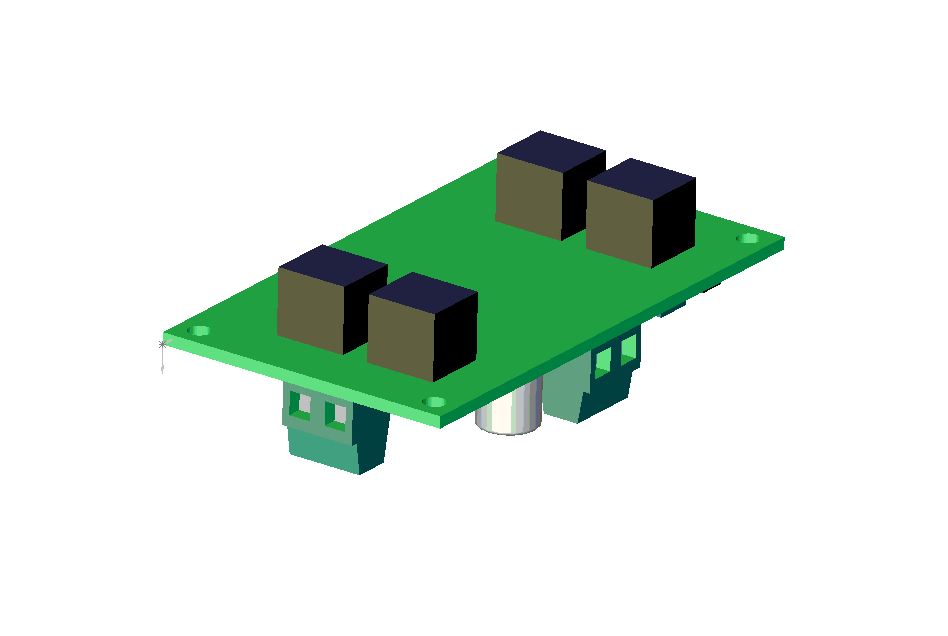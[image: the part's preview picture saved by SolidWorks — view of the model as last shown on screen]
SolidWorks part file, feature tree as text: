
SOLIDWORKS PART (.sldprt)
format: sldprt  version: not decoded by parser v0  size: 579,072 bytes
history: native  units: mm
features: sketch x24, extrude x15, cut_extrude x9, fillet x1, chamfer x1 (+8 scaffold rows collapsed)
feature tree (58):
  scaffold x8  (default folders/planes/origin — collapsed)
  sketch  "Sketch1"  dims[c1.D3=3.048mm c1.D4=3.05mm c1.D5=3.05mm c1.D6=3.05mm c2.D3=3.05mm c2.D1=69.0mm c2.D2=40.15mm c2.D7=3.05mm c2.D8=3.05mm c2.D9=3.05mm c2.D10=3.05mm]
  extrude  "Base-Extrude"  Depth=1.5748mm
  sketch  "Sketch2"  dims[c1.D1=12.7mm c1.D2=10.1mm c1.D3=10.1mm c1.D4=10.1mm c1.D5=8.1mm c1.D6=8.1mm c1.D7=8.1mm c1.D8=12.7mm c1.D9=28.5mm c2.D5=0.1mm c2.D6=0.1mm c2.D10=0.1mm c2.D11=8.0mm c2.D7=8.0mm c2.D12=8.0mm]
  extrude  "Boss-Extrude1"  Depth=9.94mm
  sketch  "Sketch3"  dims[c1.D1=4.3mm c1.D2=0.96mm c1.D3=1.7mm c1.D4=7.5mm c1.D5=1.45mm c1.D6=1.45mm c1.D7=7.5mm c1.D8=0.96mm c1.D9=0.96mm c2.D9=90.0deg c3.D9=1.7mm c3.D10=4.3mm]
  cut_extrude  "Cut-Extrude1"  [1 undecoded]
  sketch  "Sketch4"  dims[D1=0.96mm D2=4.3mm D3=1.7mm D4=1.45mm D5=7.5mm]
  cut_extrude  "Cut-Extrude2"  [1 undecoded]
  sketch  "Sketch5"  dims[D2=3.7mm D4=3.7mm D11=3.7mm D12=3.7mm D17=3.7mm D18=3.7mm D1=2.7mm D3=2.42mm D5=2.7mm D6=2.42mm D7=2.42mm D8=2.42mm D9=2.7mm D10=2.7mm D13=2.7mm D14=2.7mm D15=2.42mm D16=2.42mm]
  cut_extrude  "Cut-Extrude3"  Depth=2mm
  sketch  "Sketch6"  dims[D1=3.1mm D2=3.1mm D3=3.1mm D4=3.1mm D5=3.1mm D6=3.1mm]
  extrude  "Boss-Extrude4"  [1 undecoded]
  sketch  "Sketch7"  dims[c1.D7=~3.256358mm c1.D8=~3.313702mm c1.D1=0.5mm c1.D2=0.5mm c1.D3=0.5mm c1.D4=0.5mm c1.D5=10.1mm c2.D5=40.0deg c2.D6=~2.93428mm c3.D6=55.0deg c3.D2=0.5mm c4.D6=~4.719132mm c5.D6=55.0deg]
  cut_extrude  "Cut-Extrude4"  Depth=1.2mm
  sketch  "Sketch8"  dims[c1.D1=~3.324113mm c1.D2=~3.344496mm c1.D3=0.5mm c1.D4=1.0mm c1.D5=~4.793274mm c2.D5=128.0deg c2.D6=0.5mm c2.D7=1.0mm c2.D8=~4.589517mm c3.D8=~60.168045deg]
  cut_extrude  "Cut-Extrude5"  Depth=1.2mm
  sketch  "Sketch10"  dims[c1.D1=~3.328408mm c1.D2=~3.418532mm c1.D3=0.5mm c1.D4=1.0mm c1.D5=0.5mm c1.D6=1.0mm c1.D7=~4.415311mm c2.D7=50.0deg c2.D8=~4.611922mm c3.D8=48.0deg]
  cut_extrude  "Cut-Extrude6"  Depth=1.2mm
  sketch  "Sketch11"  dims[c1.D1=1.0mm c1.D2=1.0mm c1.D3=2.0mm c1.D4=1.5mm c1.D5=1.5mm c1.D6=1.0mm c1.D7=1.0mm c1.D8=3.0mm c2.D3=3.0mm]
  cut_extrude  "Cut-Extrude7"  Depth=2mm
  sketch  "Sketch12"  dims[D1=1.0mm D2=1.0mm D3=1.5mm D4=1.5mm D5=1.0mm D6=1.0mm D7=3.0mm D8=3.0mm]
  cut_extrude  "Cut-Extrude8"  Depth=2mm
  sketch  "Sketch13"  dims[D1=1.0mm D2=1.0mm D3=1.0mm D4=1.0mm D5=1.5mm D6=1.5mm D7=3.0mm D8=3.0mm]
  cut_extrude  "Cut-Extrude9"  Depth=2mm
  sketch  "Sketch14"  dims[D3=8.0mm D1=8.23mm D2=25.4mm]
  extrude  "Boss-Extrude5"  Depth=10mm
  fillet  "Fillet1"  Radius=0.5mm
  sketch  "Sketch15"  dims[D1=7.82mm D2=7.0mm D3=5.0mm D4=1.65mm D5=2.0mm D6=28.7mm D7=5.0mm D8=10.42mm]
  extrude  "Boss-Extrude6"  Depth=2.46mm
  sketch  "Sketch16"  dims[D1=0.61mm D2=0.61mm D3=0.61mm D4=0.61mm D5=2.54mm D6=2.54mm D7=2.54mm D8=0.61mm D9=1.065mm D10=0.925mm D11=0.61mm D12=0.61mm D13=0.61mm D14=0.61mm D15=0.61mm D16=0.61mm D17=2.54mm D18=2.54mm D19=2.54mm D20=0.93mm D21=1.07mm D22=2.54mm]
  extrude  "Boss-Extrude7"  Depth=6mm
  chamfer  "Chamfer2"  Distance=0.25mm Angle=45deg
  sketch  "Sketch17"  dims[D1=8.83mm D2=10.93mm D3=9.54mm D4=9.54mm D5=8.7mm D6=8.7mm D7=6.62mm D8=7.66mm D9=8.7mm]
  extrude  "Boss-Extrude8"  Depth=8.7mm
  sketch  "Sketch19"  dims[c1.D1=8.07mm c1.D2=3.66mm c1.D3=4.2mm c1.D4=3.2mm c1.D5=13.06mm c1.D6=6.53mm c1.D7=8.6mm c1.D8=3.5mm c2.D5=13.6mm c2.D7=8.6mm c2.D4=3.2mm c2.D1=8.07mm]
  extrude  "Boss-Extrude9"  Depth=2.58mm
  sketch  "Sketch20"  dims[D1=16.02mm D2=7.0mm D3=7.0mm D4=33.0mm]
  extrude  "Boss-Extrude10"  Depth=1mm
  sketch  "Sketch21"  dims[D1=1.15mm D2=1.15mm D3=1.15mm D4=5.08mm D5=5.08mm D6=2.54mm D7=14.22mm]
  extrude  "Boss-Extrude11"  Depth=7mm
  sketch  "Sketch22"  dims[D1=1.15mm D2=1.15mm D3=1.15mm D4=2.54mm]
  extrude  "Boss-Extrude12"  Depth=7mm
  sketch  "Sketch23"  dims[D1=1.15mm D2=1.15mm D3=1.15mm D4=2.54mm]
  extrude  "Boss-Extrude13"  Depth=7mm
  sketch  "Sketch24"  dims[D1=12.73mm D2=12.73mm D3=16.17mm D4=16.17mm D5=3.2mm D6=3.2mm D7=3.2mm D8=3.2mm D9=15.0mm D10=14.5mm D11=1.6mm D12=2.64mm]
  extrude  "Boss-Extrude14"  Depth=1mm
  sketch  "Sketch25"  dims[D1=22.0mm D2=1.75mm D3=1.75mm D4=3.35mm D5=3.35mm D6=9.29mm D7=9.29mm D8=28.4mm D9=23.0mm D10=1.75mm D11=3.35mm D12=22.15mm D13=3.35mm D14=3.35mm D15=1.75mm D16=1.75mm D17=25.0mm D18=16.57mm D19=10.9mm]
  extrude  "Boss-Extrude15"  Depth=1.63mm
  sketch  "Sketch26"  dims[c1.D1=1.0mm c1.D2=~2.103898mm c1.D3=2.01mm c1.D4=1.0mm c1.D5=0.7mm c2.D2=0.7mm]
  extrude  "Boss-Extrude16"  Depth=6.5mm
decode coverage: 47 of 50 modeling features carry decoded parameters
note: ~ marks probable driven/reference dimensions
note: 3 parameter values undecoded
summary: no parameter record found for 3 features
note: suppression state not decoded; provenance and decode notes live in map.json
